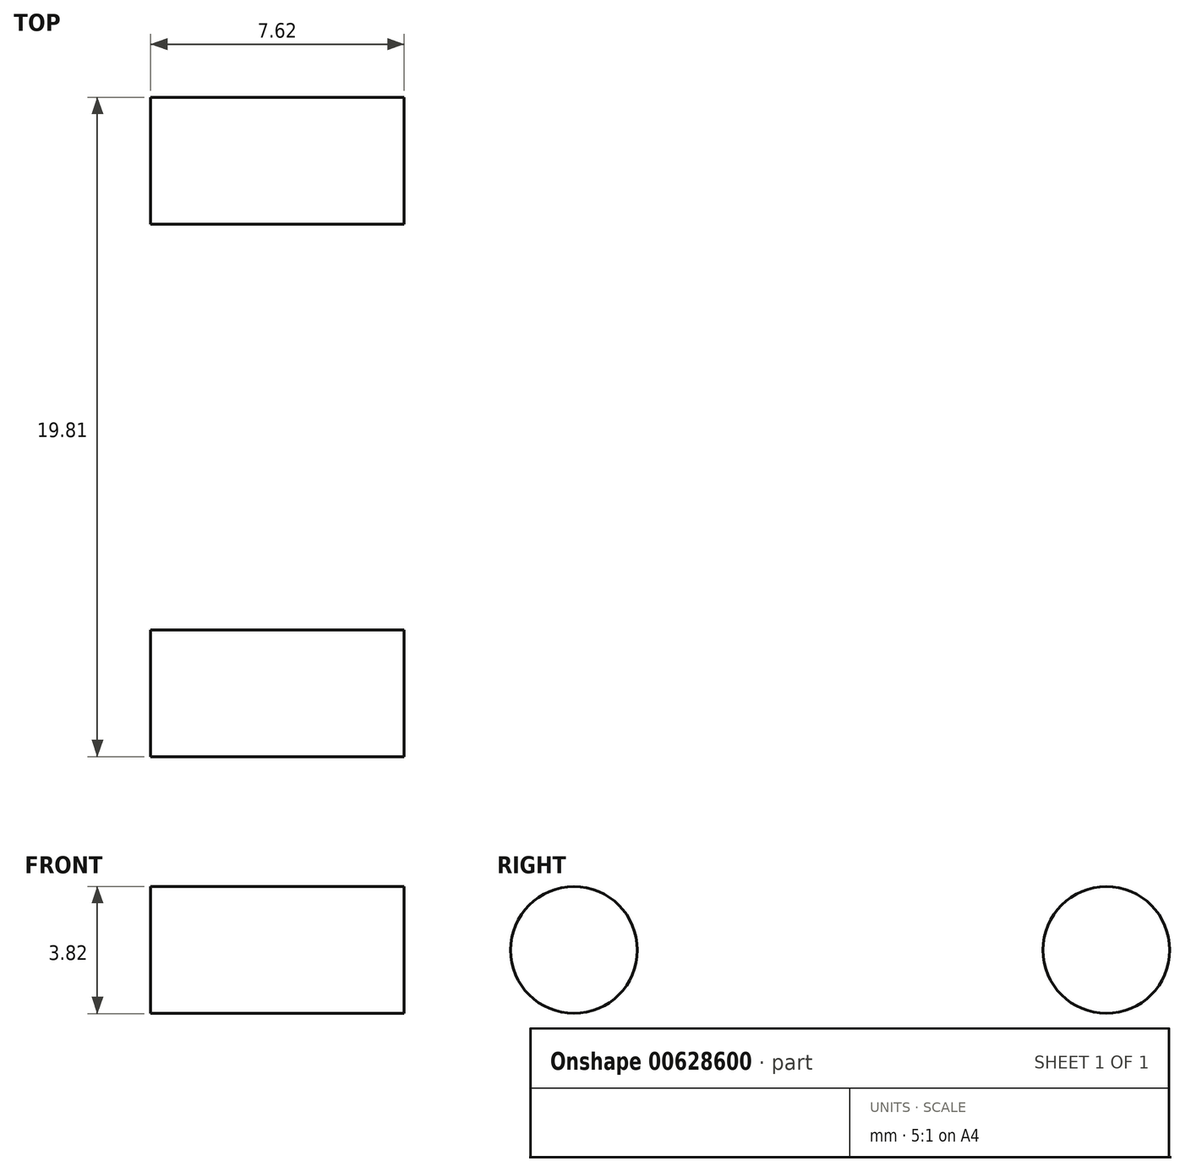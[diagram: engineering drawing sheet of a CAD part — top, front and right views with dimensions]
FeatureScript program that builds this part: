
annotation { "Feature Type Name" : "Feature", "Feature Type Description" : "" }
export const myFeature = defineFeature(function(context is Context, id is Id, definition is map)
    precondition{}
    {
        {
            var Q0;
            Q0=qCreatedBy(makeId("Front.planeOp"),FACE);
            var sketch = newSketch(context, id + "F0", { "sketchPlane" : qUnion([Q0])});
            skLineSegment(sketch, "E0", {"start": v(0, 0) * mm, "end": v(0, 76.2) * mm});
            skLineSegment(sketch, "E1", {"start": v(0, 76.2) * mm, "end": v(7.62, 76.2) * mm});
            skLineSegment(sketch, "E2", {"start": v(7.62, 76.2) * mm, "end": v(7.62, 0) * mm});
            skLineSegment(sketch, "E3", {"start": v(7.62, 0) * mm, "end": v(0, 0) * mm});
            skSolve(sketch);
        }
        {
            var Q0;
            Q0=makeQuery(id+"F0.imprint","IMPRINT",FACE,{"disambiguationData":[TD([[makeQuery(id+"F0.imprint","IMPRINT",EDGE,{"derivedFrom":sQuery(id+"F0.wireOp",EDGE,"E0")}),-1.0]])]});
            extrude(context, id + "F1", {"entities" : qUnion([Q0]), "depth" : 101.6 * mm, "offsetDistance" : 25.4 * mm});
        }
        {
            var Q0;
            Q0=makeQuery(id+"F1.opExtrude","SWEPT_FACE",FACE,{"disambiguationData":[OSD([sQuery(id+"F0.wireOp",EDGE,"E0")])]});
            var sketch = newSketch(context, id + "F2", { "sketchPlane" : qUnion([Q0])});
            skLineSegment(sketch, "E4", {"start": v(50.8, 38.1) * mm, "end": v(50.8, 76.2) * mm});
            skPoint(sketch, "E4.startSnap0", {"position": v(101.6, 38.1) * mm});
            skPoint(sketch, "E4.startSnap1", {"position": v(50.8, 76.2) * mm});
            skLineSegment(sketch, "E5", {"start": v(50.8, 38.1) * mm, "end": v(82.8, 38.1) * mm});
            skLineSegment(sketch, "E6", {"start": v(82.8, 38.1) * mm, "end": v(90.8, 38.1) * mm});
            skLineSegment(sketch, "E7", {"start": v(82.8, 38.1) * mm, "end": v(74.8, 38.1) * mm});
            skCircle(sketch, "E8", {"center": v(90.8, 38.1) * mm, "radius": 1.9 * mm});
            skCircle(sketch, "E9", {"center": v(74.8, 38.1) * mm, "radius": 1.9 * mm});
            skCircle(sketch, "E10.MirrorC", {"center": v(26.8, 38.1) * mm, "radius": 1.9 * mm});
            skCircle(sketch, "E11.MirrorC", {"center": v(10.8, 38.1) * mm, "radius": 1.9 * mm});
            skSolve(sketch);
        }
        {
            var Q0;
            Q0=makeQuery(id+"F2.imprint","IMPRINT",FACE,{"disambiguationData":[TD([[makeQuery(id+"F2.imprint","IMPRINT",EDGE,{"derivedFrom":sQuery(id+"F2.wireOp",EDGE,"E8")}),1.0]])]});
            var Q1;
            {var subQ0=sQuery(id+"F2.wireOp",EDGE,"E7");var subQ1=sQuery(id+"F2.wireOp",EDGE,"E5");var subQ2=makeQuery(id+"F2.imprint","INTERSECT",VERTEX,{"derivedFrom":[subQ1,subQ0]});Q1=makeQuery(id+"F2.imprint","IMPRINT",FACE,{"disambiguationData":[TD([[makeQuery(id+"F2.imprint","IMPRINT",EDGE,{"disambiguationData":[TD([[subQ2,1.0]])],"derivedFrom":subQ1}),1.0]])]});}
            var Q2;
            {var subQ0=sQuery(id+"F2.wireOp",EDGE,"E7");var subQ1=sQuery(id+"F2.wireOp",EDGE,"E5");var subQ2=makeQuery(id+"F2.imprint","INTERSECT",VERTEX,{"derivedFrom":[subQ1,subQ0]});Q2=makeQuery(id+"F2.imprint","IMPRINT",FACE,{"disambiguationData":[TD([[makeQuery(id+"F2.imprint","IMPRINT",EDGE,{"disambiguationData":[TD([[subQ2,1.0]])],"derivedFrom":subQ1}),-1.0]])]});}
            var Q3;
            Q3=makeQuery(id+"F2.imprint","IMPRINT",FACE,{"disambiguationData":[TD([[makeQuery(id+"F2.imprint","IMPRINT",EDGE,{"derivedFrom":sQuery(id+"F2.wireOp",EDGE,"E10.MirrorC")}),-1.0]])]});
            var Q4;
            Q4=makeQuery(id+"F2.imprint","IMPRINT",FACE,{"disambiguationData":[TD([[makeQuery(id+"F2.imprint","IMPRINT",EDGE,{"derivedFrom":sQuery(id+"F2.wireOp",EDGE,"E11.MirrorC")}),-1.0]])]});
            extrude(context, id + "F3", {"entities" : qUnion([Q0, Q1, Q2, Q3, Q4]), "operationType" : NewBodyOperationType.REMOVE, "oppositeDirection" : true, "depth" : 25.4 * mm, "offsetDistance" : 25.4 * mm});
        }
    });
